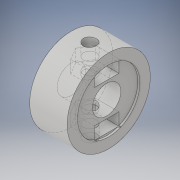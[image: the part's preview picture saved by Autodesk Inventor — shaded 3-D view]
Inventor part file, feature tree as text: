
AUTODESK INVENTOR PART (.ipt)
format: ipt  version: 2019 (Build 230136000, 136)  size: 171,520 bytes
history: native  units: mm
features: sketch x4, extrude x3, plane x2, hole x1, mirror x1
ambient origin geometry x8: Origin, YZ Plane, XZ Plane, XY Plane, X Axis, Y Axis, Z Axis, Center Point
bodies: Body1 (feature_tree)
feature tree (11):
  extrude  "Extrusion7"  Depth=6.8mm
  extrude  "Extrusion8"  Depth=15.0mm
  plane  "Work Plane3"
  extrude  "Extrusion9"  Depth=5.5mm
  plane  "Work Plane4"
  hole  "Hole2"  [1 undecoded]
  mirror  "Mirror2"
  sketch  "Sketch9"  dims[d31=20.0mm d32=6.8mm]
  sketch  "Sketch10"  dims[d33=9.0mm d34=0.0mm d35=15.0mm]
  sketch  "Sketch11"  dims[d36=0.5mm d37=0.0mm d38=5.5mm]
  sketch  "Sketch12"  dims[d39=5.9mm d40=3.0mm d41=0.0mm d42=4.5mm d43=3.1mm d44=6.0mm d45=4.0mm d46=2.0mm d47=90.0deg d48=10.0mm d49=0.0mm]
note: 1 required parameter value undecoded (feature->parameter linkage not recoverable at this tier; creation-order binding heuristic only, values carry confidence <= 0.55)
